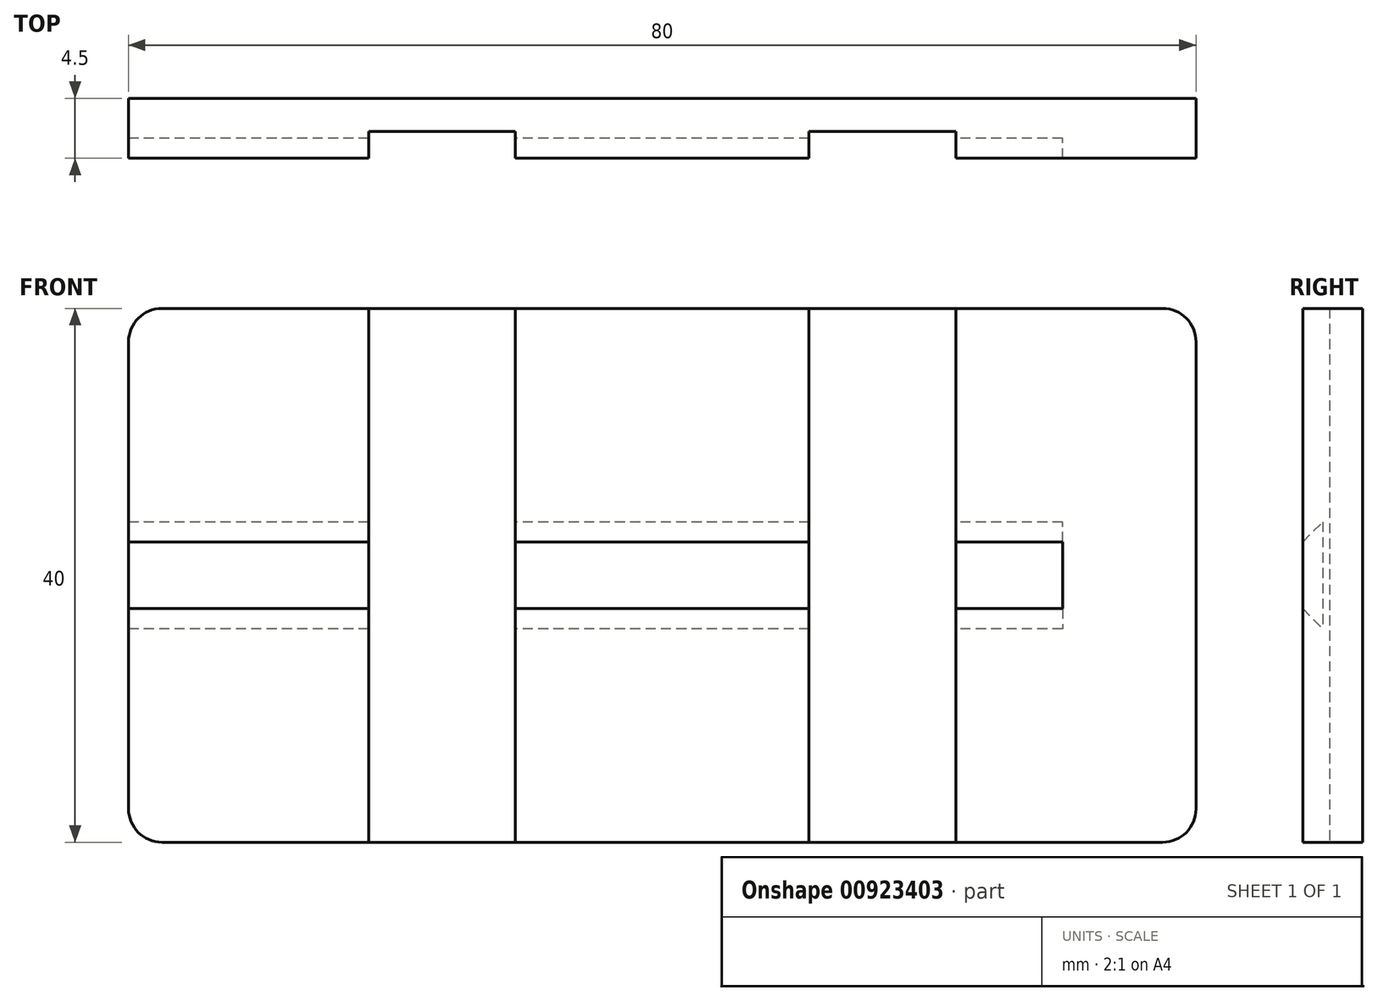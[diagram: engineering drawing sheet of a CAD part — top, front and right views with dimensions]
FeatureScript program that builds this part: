
annotation { "Feature Type Name" : "Feature", "Feature Type Description" : "" }
export const myFeature = defineFeature(function(context is Context, id is Id, definition is map)
    precondition{}
    {
        {
            var Q0;
            Q0=qCreatedBy(makeId("Front.planeOp"),FACE);
            var sketch = newSketch(context, id + "F0", { "sketchPlane" : qUnion([Q0])});
            skLineSegment(sketch, "E0", {"start": v(0, 50.73) * mm, "end": v(0, -52.35) * mm, "construction": true});
            skLineSegment(sketch, "E1", {"start": v(-81.92, 0) * mm, "end": v(92.05, 0) * mm, "construction": true});
            skLineSegment(sketch, "E2.bottom", {"start": v(-40, 20) * mm, "end": v(40, 20) * mm});
            skLineSegment(sketch, "E2.top", {"start": v(-40, -20) * mm, "end": v(40, -20) * mm});
            skLineSegment(sketch, "E2.left", {"start": v(-40, 20) * mm, "end": v(-40, -20) * mm});
            skLineSegment(sketch, "E2.right", {"start": v(40, 20) * mm, "end": v(40, -20) * mm});
            skPoint(sketch, "E2.middle", {"position": v(0, 0) * mm});
            skLineSegment(sketch, "E3", {"start": v(-11, 51.13) * mm, "end": v(-11, -50.84) * mm, "construction": true});
            skLineSegment(sketch, "E4", {"start": v(11, 51.13) * mm, "end": v(11, -51.83) * mm, "construction": true});
            skLineSegment(sketch, "E5.bottom", {"start": v(-11, 20) * mm, "end": v(-22, 20) * mm});
            skLineSegment(sketch, "E5.top", {"start": v(-11, -20) * mm, "end": v(-22, -20) * mm});
            skLineSegment(sketch, "E5.left", {"start": v(-11, 20) * mm, "end": v(-11, -20) * mm});
            skLineSegment(sketch, "E5.right", {"start": v(-22, 20) * mm, "end": v(-22, -20) * mm});
            skLineSegment(sketch, "E6.bottom", {"start": v(11, 20) * mm, "end": v(22, 20) * mm});
            skLineSegment(sketch, "E6.top", {"start": v(11, -20) * mm, "end": v(22, -20) * mm});
            skLineSegment(sketch, "E6.left", {"start": v(11, 20) * mm, "end": v(11, -20) * mm});
            skLineSegment(sketch, "E6.right", {"start": v(22, 20) * mm, "end": v(22, -20) * mm});
            skSolve(sketch);
        }
        {
            var Q0;
            Q0 = qSketchRegion(id + "F0", true);
            extrude(context, id + "F1", {"entities" : qUnion([Q0]), "oppositeDirection" : true, "depth" : 4.5 * mm, "offsetDistance" : 25 * mm});
        }
        {
            var Q0;
            Q0=qCreatedBy(makeId("Front.planeOp"),FACE);
            var sketch = newSketch(context, id + "F2", { "sketchPlane" : qUnion([Q0])});
            skLineSegment(sketch, "E7", {"start": v(0, 26.46) * mm, "end": v(0, -27.4) * mm, "construction": true});
            skLineSegment(sketch, "E8", {"start": v(-11, 25.9) * mm, "end": v(-11, -27.29) * mm, "construction": true});
            skLineSegment(sketch, "E9", {"start": v(11, 26.24) * mm, "end": v(11, -27.4) * mm, "construction": true});
            skLineSegment(sketch, "E10", {"start": v(-44.18, 0) * mm, "end": v(45, 0) * mm, "construction": true});
            skLineSegment(sketch, "E11", {"start": v(-44.18, 20) * mm, "end": v(44.66, 20) * mm, "construction": true});
            skLineSegment(sketch, "E12", {"start": v(-44.18, -20) * mm, "end": v(45, -20) * mm, "construction": true});
            skLineSegment(sketch, "E13.bottom", {"start": v(-11, 20) * mm, "end": v(-22, 20) * mm});
            skLineSegment(sketch, "E13.top", {"start": v(-11, -20) * mm, "end": v(-22, -20) * mm});
            skLineSegment(sketch, "E13.left", {"start": v(-11, 20) * mm, "end": v(-11, -20) * mm});
            skLineSegment(sketch, "E13.right", {"start": v(-22, 20) * mm, "end": v(-22, -20) * mm});
            skLineSegment(sketch, "E14.bottom", {"start": v(11, 20) * mm, "end": v(22, 20) * mm});
            skLineSegment(sketch, "E14.top", {"start": v(11, -20) * mm, "end": v(22, -20) * mm});
            skLineSegment(sketch, "E14.left", {"start": v(11, 20) * mm, "end": v(11, -20) * mm});
            skLineSegment(sketch, "E14.right", {"start": v(22, 20) * mm, "end": v(22, -20) * mm});
            skSolve(sketch);
        }
        {
            var Q0;
            Q0 = qSketchRegion(id + "F2", true);
            extrude(context, id + "F3", {"entities" : qUnion([Q0]), "operationType" : NewBodyOperationType.REMOVE, "oppositeDirection" : true, "depth" : 2 * mm, "offsetDistance" : 25 * mm});
        }
        {
            var Q0;
            Q0=makeQuery(id+"F1.opExtrude","SWEPT_FACE",FACE,{"disambiguationData":[OSD([sQuery(id+"F0.wireOp",EDGE,"E2.left")])]});
            var sketch = newSketch(context, id + "F4", { "sketchPlane" : qUnion([Q0])});
            skLineSegment(sketch, "E15", {"start": v(15.2, 0) * mm, "end": v(-14.12, 0) * mm, "construction": true});
            skPoint(sketch, "E15.endSnap0", {"position": v(-4.5, 0) * mm});
            skLineSegment(sketch, "E16", {"start": v(15.04, 2.5) * mm, "end": v(-10.92, 2.5) * mm, "construction": true});
            skLineSegment(sketch, "E17", {"start": v(-10.63, 4) * mm, "end": v(12.01, 4) * mm, "construction": true});
            skLineSegment(sketch, "E18", {"start": v(0, 0) * mm, "end": v(0, 2.5) * mm});
            skLineSegment(sketch, "E19", {"start": v(0, 2.5) * mm, "end": v(-1.5, 4) * mm});
            skLineSegment(sketch, "E20", {"start": v(-1.5, 4) * mm, "end": v(-1.5, 0) * mm});
            skLineSegment(sketch, "E21.MirrorCS", {"start": v(0, -2.5) * mm, "end": v(-1.5, -4) * mm});
            skLineSegment(sketch, "E22.MirrorCS", {"start": v(0, 0) * mm, "end": v(0, -2.5) * mm});
            skLineSegment(sketch, "E23.MirrorCS", {"start": v(-1.5, -4) * mm, "end": v(-1.5, 0) * mm});
            skSolve(sketch);
        }
        {
            var Q0;
            Q0 = qSketchRegion(id + "F4", true);
            extrude(context, id + "F5", {"entities" : qUnion([Q0]), "operationType" : NewBodyOperationType.REMOVE, "oppositeDirection" : true, "depth" : 70 * mm, "offsetDistance" : 25 * mm});
        }
        {
            var Q0;
            Q0=makeQuery(id+"F3.boolean.opBoolean","COPY",EDGE,{"derivedFrom":makeQuery(id+"F3.opExtrude","CAP_EDGE",EDGE,{"disambiguationData":[OSD([sQuery(id+"F2.wireOp",EDGE,"E13.bottom")])],"isStart":false})});
            var Q1;
            Q1=makeQuery(id+"F3.boolean.opBoolean","COPY",EDGE,{"derivedFrom":makeQuery(id+"F3.opExtrude","CAP_EDGE",EDGE,{"disambiguationData":[OSD([sQuery(id+"F2.wireOp",EDGE,"E14.bottom")])],"isStart":false})});
            var Q2;
            Q2=makeQuery(id+"F3.boolean.opBoolean","COPY",EDGE,{"derivedFrom":makeQuery(id+"F3.opExtrude","CAP_EDGE",EDGE,{"disambiguationData":[OSD([sQuery(id+"F2.wireOp",EDGE,"E14.top")])],"isStart":false})});
            var Q3;
            Q3=makeQuery(id+"F3.boolean.opBoolean","COPY",EDGE,{"derivedFrom":makeQuery(id+"F3.opExtrude","CAP_EDGE",EDGE,{"disambiguationData":[OSD([sQuery(id+"F2.wireOp",EDGE,"E13.top")])],"isStart":false})});
            var Q4;
            Q4=makeQuery(id+"F1.opExtrude","SWEPT_EDGE",EDGE,{"disambiguationData":[OSD([sQuery(id+"F0.wireOp",EDGE,"E2.bottom"),sQuery(id+"F0.wireOp",EDGE,"E2.left")])]});
            var Q5;
            Q5=makeQuery(id+"F1.opExtrude","SWEPT_EDGE",EDGE,{"disambiguationData":[OSD([sQuery(id+"F0.wireOp",EDGE,"E2.top"),sQuery(id+"F0.wireOp",EDGE,"E2.left")])]});
            var Q6;
            Q6=makeQuery(id+"F1.opExtrude","SWEPT_EDGE",EDGE,{"disambiguationData":[OSD([sQuery(id+"F0.wireOp",EDGE,"E2.top"),sQuery(id+"F0.wireOp",EDGE,"E2.right")])]});
            var Q7;
            Q7=makeQuery(id+"F1.opExtrude","SWEPT_EDGE",EDGE,{"disambiguationData":[OSD([sQuery(id+"F0.wireOp",EDGE,"E2.bottom"),sQuery(id+"F0.wireOp",EDGE,"E2.right")])]});
            fillet(context, id + "F6", {"entities" : qUnion([Q0, Q1, Q2, Q3, Q4, Q5, Q6, Q7]), "radius" : 2.5 * mm, "tangentPropagation" : true, "allowEdgeOverflow" : false});
        }
    });
